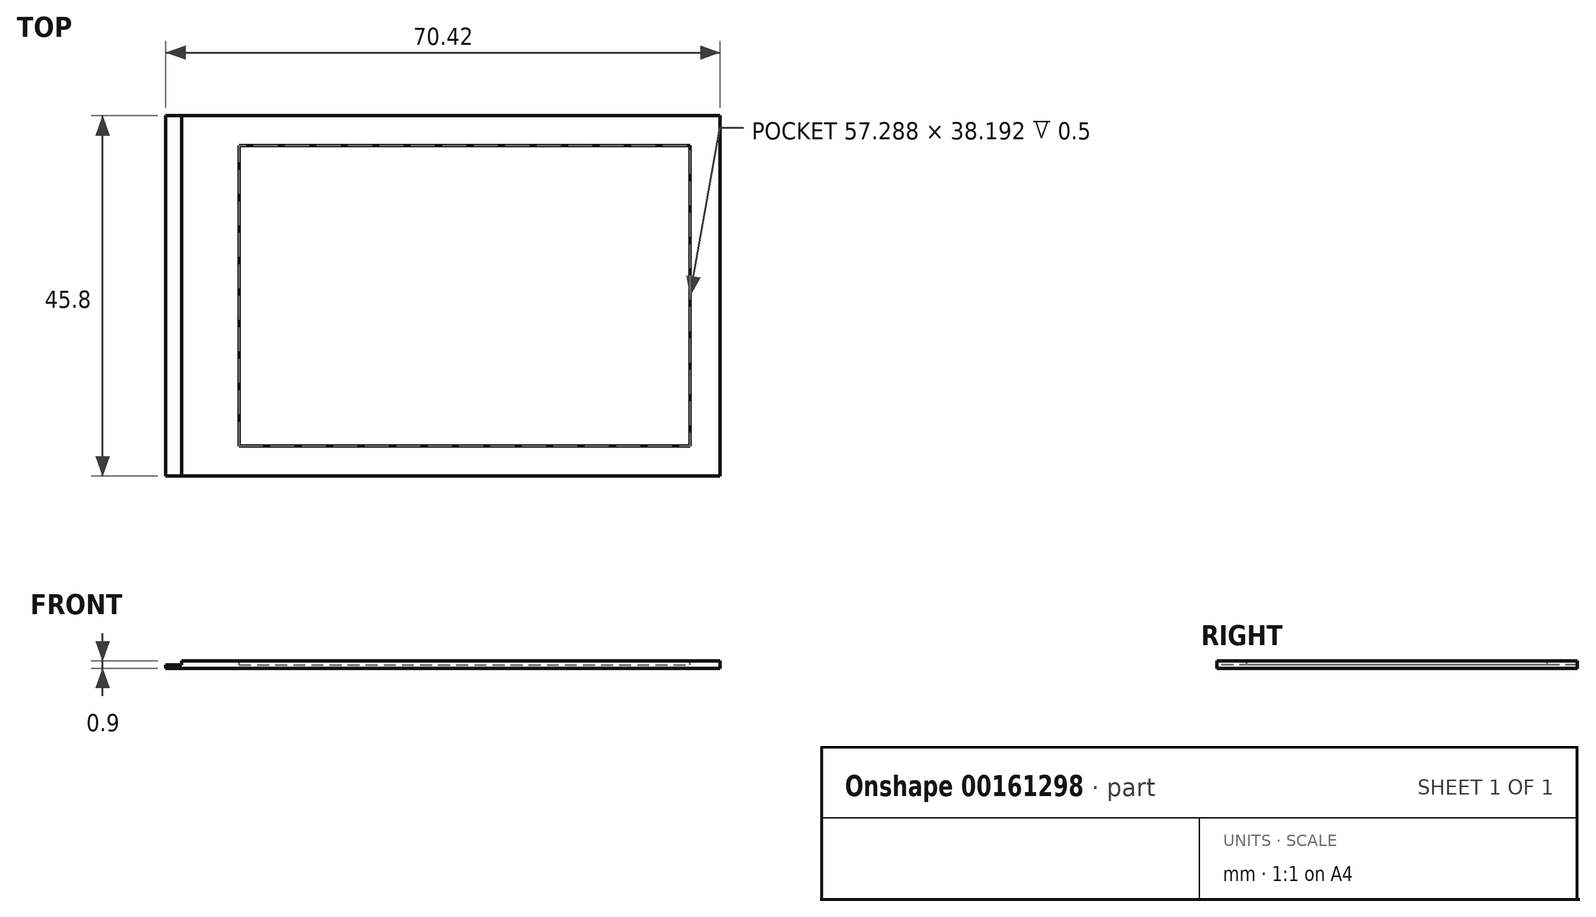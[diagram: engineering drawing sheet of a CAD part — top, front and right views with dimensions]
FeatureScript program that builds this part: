
annotation { "Feature Type Name" : "Feature", "Feature Type Description" : "" }
export const myFeature = defineFeature(function(context is Context, id is Id, definition is map)
    precondition{}
    {
        {
            var Q0;
            Q0=qCreatedBy(makeId("Top.planeOp"),FACE);
            var sketch = newSketch(context, id + "F0", { "sketchPlane" : qUnion([Q0])});
            skLineSegment(sketch, "E0.bottom", {"start": v(35.2, 22.9) * mm, "end": v(-35.2, 22.9) * mm});
            skLineSegment(sketch, "E0.top", {"start": v(35.2, -22.9) * mm, "end": v(-35.2, -22.9) * mm});
            skLineSegment(sketch, "E0.left", {"start": v(35.2, 22.9) * mm, "end": v(35.2, -22.9) * mm});
            skLineSegment(sketch, "E0.right", {"start": v(-35.2, 22.9) * mm, "end": v(-35.2, -22.9) * mm});
            skPoint(sketch, "E0.middle", {"position": v(0, 0) * mm});
            skSolve(sketch);
        }
        {
            var Q0;
            Q0 = qSketchRegion(id + "F0", true);
            extrude(context, id + "F1", {"entities" : qUnion([Q0]), "depth" : .9 * mm});
        }
        {
            var Q0;
            Q0=makeQuery(id+"F1.opExtrude","CAP_FACE",FACE,{"disambiguationData":[OSD([sQuery(id+"F0.wireOp",EDGE,"E0.bottom"),sQuery(id+"F0.wireOp",EDGE,"E0.top"),sQuery(id+"F0.wireOp",EDGE,"E0.left"),sQuery(id+"F0.wireOp",EDGE,"E0.right")])],"isStart":false});
            var sketch = newSketch(context, id + "F2", { "sketchPlane" : qUnion([Q0])});
            skLineSegment(sketch, "E1.bottom", {"start": v(-25.9, 19.1) * mm, "end": v(31.4, 19.1) * mm});
            skLineSegment(sketch, "E1.top", {"start": v(-25.9, -19.1) * mm, "end": v(31.4, -19.1) * mm});
            skLineSegment(sketch, "E1.left", {"start": v(-25.9, 19.1) * mm, "end": v(-25.9, -19.1) * mm});
            skLineSegment(sketch, "E1.right", {"start": v(31.4, 19.1) * mm, "end": v(31.4, -19.1) * mm});
            skSolve(sketch);
        }
        {
            var Q0;
            Q0=makeQuery(id+"F2.imprint","IMPRINT",FACE,{"disambiguationData":[TD([[makeQuery(id+"F2.imprint","IMPRINT",EDGE,{"derivedFrom":sQuery(id+"F2.wireOp",EDGE,"E1.bottom")}),-1.0]])]});
            extrude(context, id + "F3", {"entities" : qUnion([Q0]), "operationType" : NewBodyOperationType.REMOVE, "oppositeDirection" : true, "depth" : .5 * mm});
        }
        {
            var Q0;
            Q0=makeQuery(id+"F1.opExtrude","CAP_FACE",FACE,{"disambiguationData":[OSD([sQuery(id+"F0.wireOp",EDGE,"E0.bottom"),sQuery(id+"F0.wireOp",EDGE,"E0.top"),sQuery(id+"F0.wireOp",EDGE,"E0.left"),sQuery(id+"F0.wireOp",EDGE,"E0.right")])],"isStart":false});
            var sketch = newSketch(context, id + "F4", { "sketchPlane" : qUnion([Q0])});
            skLineSegment(sketch, "E2.bottom", {"start": v(-35.2, 22.9) * mm, "end": v(-33.2, 22.9) * mm});
            skLineSegment(sketch, "E2.top", {"start": v(-35.2, -22.9) * mm, "end": v(-33.2, -22.9) * mm});
            skLineSegment(sketch, "E2.left", {"start": v(-35.2, 22.9) * mm, "end": v(-35.2, -22.9) * mm});
            skLineSegment(sketch, "E2.right", {"start": v(-33.2, 22.9) * mm, "end": v(-33.2, -22.9) * mm});
            skSolve(sketch);
        }
        {
            var Q0;
            Q0=makeQuery(id+"F4.imprint","IMPRINT",FACE,{"disambiguationData":[TD([[makeQuery(id+"F4.imprint","IMPRINT",EDGE,{"derivedFrom":sQuery(id+"F4.wireOp",EDGE,"E2.bottom")}),1.0]])]});
            extrude(context, id + "F5", {"entities" : qUnion([Q0]), "operationType" : NewBodyOperationType.REMOVE, "oppositeDirection" : true, "depth" : .5 * mm});
        }
    });
